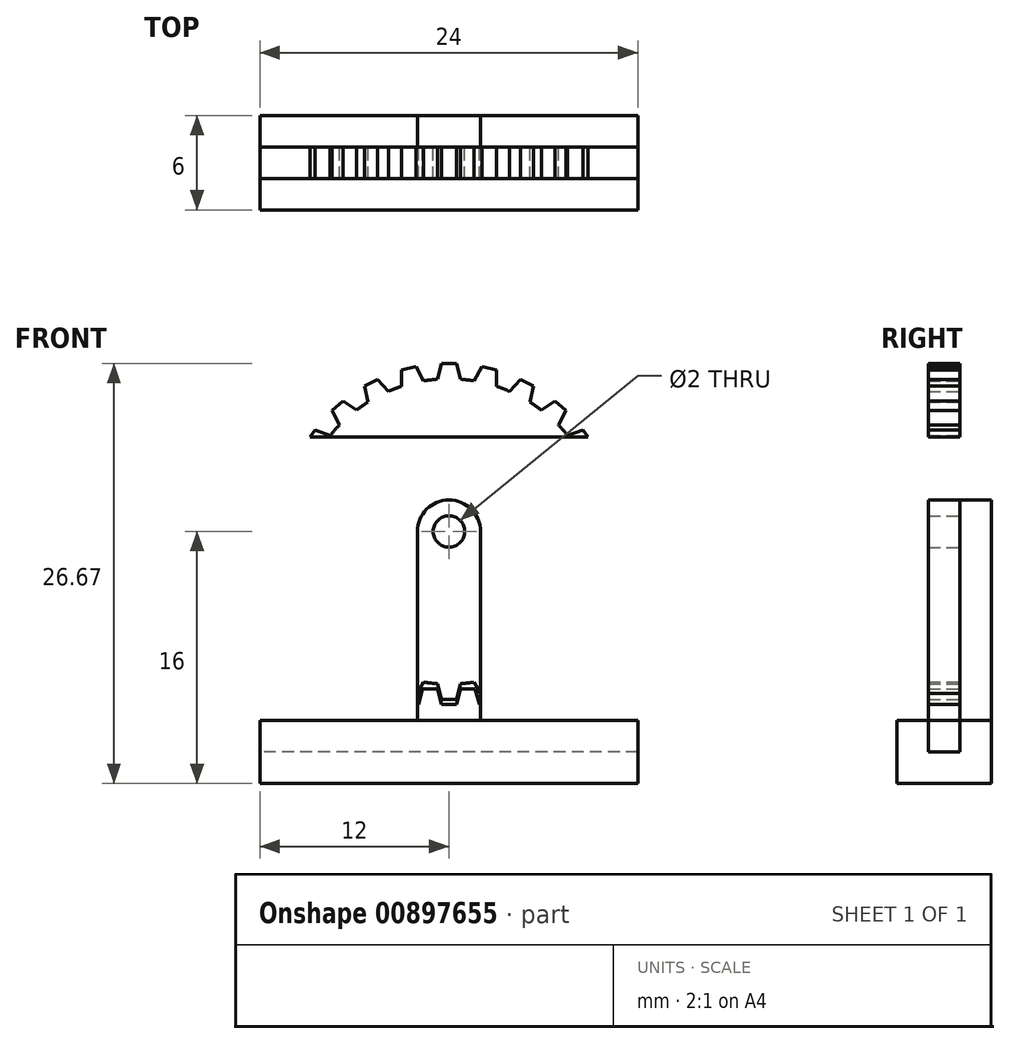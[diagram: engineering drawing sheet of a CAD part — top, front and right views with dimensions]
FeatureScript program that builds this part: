
annotation { "Feature Type Name" : "Feature", "Feature Type Description" : "" }
export const myFeature = defineFeature(function(context is Context, id is Id, definition is map)
    precondition{}
    {
        {
            var Q0;
            Q0=qCreatedBy(makeId("Right.planeOp"),FACE);
            var sketch = newSketch(context, id + "F0", { "sketchPlane" : qUnion([Q0])});
            skLineSegment(sketch, "E0", {"start": v(0, 2) * mm, "end": v(-2, 2) * mm});
            skLineSegment(sketch, "E1", {"start": v(-2, 2) * mm, "end": v(-2, -2) * mm});
            skLineSegment(sketch, "E2", {"start": v(-2, -2) * mm, "end": v(4, -2) * mm});
            skLineSegment(sketch, "E3", {"start": v(4, -2) * mm, "end": v(4, 20) * mm});
            skLineSegment(sketch, "E4", {"start": v(4, 20) * mm, "end": v(2, 20) * mm});
            skLineSegment(sketch, "E5", {"start": v(2, 20) * mm, "end": v(2, 0) * mm});
            skLineSegment(sketch, "E6", {"start": v(2, 0) * mm, "end": v(0, 0) * mm});
            skLineSegment(sketch, "E7", {"start": v(0, 0) * mm, "end": v(0, 2) * mm});
            skSolve(sketch);
        }
        {
            var Q0;
            Q0 = qSketchRegion(id + "F0", true);
            extrude(context, id + "F1", {"entities" : qUnion([Q0]), "endBound" : BoundingType.SYMMETRIC, "depth" : 24 * mm, "offsetDistance" : 25 * mm});
        }
        {
            var Q0;
            Q0=makeQuery(id+"F1.opExtrude","SWEPT_FACE",FACE,{"disambiguationData":[OSD([sQuery(id+"F0.wireOp",EDGE,"E5")])]});
            var sketch = newSketch(context, id + "F2", { "sketchPlane" : qUnion([Q0])});
            skLineSegment(sketch, "E8", {"start": v(-12, 0) * mm, "end": v(12, 0) * mm});
            skLineSegment(sketch, "E9", {"start": v(-12, 3) * mm, "end": v(-11.53, 3) * mm});
            skLineSegment(sketch, "E10", {"start": v(-11.53, 3) * mm, "end": v(-11.27, 4) * mm});
            skLineSegment(sketch, "E11", {"start": v(-11.27, 4) * mm, "end": v(-10.8, 4) * mm});
            skLineSegment(sketch, "E12", {"start": v(-10.8, 4) * mm, "end": v(-10.8, 0) * mm, "construction": true});
            skLineSegment(sketch, "E13.MirrorCS", {"start": v(-10.33, 4) * mm, "end": v(-10.8, 4) * mm});
            skLineSegment(sketch, "E14.MirrorCS", {"start": v(-10.07, 3) * mm, "end": v(-10.33, 4) * mm});
            skLineSegment(sketch, "E15.MirrorCS", {"start": v(-9.6, 3) * mm, "end": v(-10.07, 3) * mm});
            skLineSegment(sketch, "E16.1.0.0", {"start": v(-9.6, 3) * mm, "end": v(-9.13, 3) * mm});
            skLineSegment(sketch, "E16.1.0.1", {"start": v(-9.13, 3) * mm, "end": v(-8.87, 4) * mm});
            skLineSegment(sketch, "E16.1.0.2", {"start": v(-8.87, 4) * mm, "end": v(-8.4, 4) * mm});
            skLineSegment(sketch, "E16.1.0.3", {"start": v(-7.93, 4) * mm, "end": v(-8.4, 4) * mm});
            skLineSegment(sketch, "E16.1.0.4", {"start": v(-7.67, 3) * mm, "end": v(-7.93, 4) * mm});
            skLineSegment(sketch, "E16.1.0.5", {"start": v(-7.2, 3) * mm, "end": v(-7.67, 3) * mm});
            skLineSegment(sketch, "E16.2.0.0", {"start": v(-7.2, 3) * mm, "end": v(-6.73, 3) * mm});
            skLineSegment(sketch, "E16.2.0.1", {"start": v(-6.73, 3) * mm, "end": v(-6.47, 4) * mm});
            skLineSegment(sketch, "E16.2.0.2", {"start": v(-6.47, 4) * mm, "end": v(-6, 4) * mm});
            skLineSegment(sketch, "E16.2.0.3", {"start": v(-5.53, 4) * mm, "end": v(-6, 4) * mm});
            skLineSegment(sketch, "E16.2.0.4", {"start": v(-5.27, 3) * mm, "end": v(-5.53, 4) * mm});
            skLineSegment(sketch, "E16.2.0.5", {"start": v(-4.8, 3) * mm, "end": v(-5.27, 3) * mm});
            skLineSegment(sketch, "E16.direction1", {"start": v(-12, 3) * mm, "end": v(-9.6, 3) * mm, "construction": true});
            skLineSegment(sketch, "E17.0.3.0", {"start": v(-4.8, 3) * mm, "end": v(-4.33, 3) * mm});
            skLineSegment(sketch, "E17.3.3.0", {"start": v(-4.33, 3) * mm, "end": v(-4.07, 4) * mm});
            skLineSegment(sketch, "E17.6.3.0", {"start": v(-4.07, 4) * mm, "end": v(-3.6, 4) * mm});
            skLineSegment(sketch, "E17.9.3.0", {"start": v(-3.13, 4) * mm, "end": v(-3.6, 4) * mm});
            skLineSegment(sketch, "E17.12.3.0", {"start": v(-2.87, 3) * mm, "end": v(-3.13, 4) * mm});
            skLineSegment(sketch, "E17.15.3.0", {"start": v(-2.4, 3) * mm, "end": v(-2.87, 3) * mm});
            skLineSegment(sketch, "E17.0.4.0", {"start": v(-2.4, 3) * mm, "end": v(-1.93, 3) * mm});
            skLineSegment(sketch, "E17.3.4.0", {"start": v(-1.93, 3) * mm, "end": v(-1.67, 4) * mm});
            skLineSegment(sketch, "E17.6.4.0", {"start": v(-1.67, 4) * mm, "end": v(-1.2, 4) * mm});
            skLineSegment(sketch, "E17.9.4.0", {"start": v(-0.73, 4) * mm, "end": v(-1.2, 4) * mm});
            skLineSegment(sketch, "E17.12.4.0", {"start": v(-0.47, 3) * mm, "end": v(-0.73, 4) * mm});
            skLineSegment(sketch, "E17.15.4.0", {"start": v(0, 3) * mm, "end": v(-0.47, 3) * mm});
            skLineSegment(sketch, "E17.0.5.0", {"start": v(0, 3) * mm, "end": v(0.47, 3) * mm});
            skLineSegment(sketch, "E17.3.5.0", {"start": v(0.47, 3) * mm, "end": v(0.73, 4) * mm});
            skLineSegment(sketch, "E17.6.5.0", {"start": v(0.73, 4) * mm, "end": v(1.2, 4) * mm});
            skLineSegment(sketch, "E17.9.5.0", {"start": v(1.67, 4) * mm, "end": v(1.2, 4) * mm});
            skLineSegment(sketch, "E17.12.5.0", {"start": v(1.93, 3) * mm, "end": v(1.67, 4) * mm});
            skLineSegment(sketch, "E17.15.5.0", {"start": v(2.4, 3) * mm, "end": v(1.93, 3) * mm});
            skLineSegment(sketch, "E17.0.6.0", {"start": v(2.4, 3) * mm, "end": v(2.87, 3) * mm});
            skLineSegment(sketch, "E17.3.6.0", {"start": v(2.87, 3) * mm, "end": v(3.13, 4) * mm});
            skLineSegment(sketch, "E17.6.6.0", {"start": v(3.13, 4) * mm, "end": v(3.6, 4) * mm});
            skLineSegment(sketch, "E17.9.6.0", {"start": v(4.07, 4) * mm, "end": v(3.6, 4) * mm});
            skLineSegment(sketch, "E17.12.6.0", {"start": v(4.33, 3) * mm, "end": v(4.07, 4) * mm});
            skLineSegment(sketch, "E17.15.6.0", {"start": v(4.8, 3) * mm, "end": v(4.33, 3) * mm});
            skLineSegment(sketch, "E17.0.7.0", {"start": v(4.8, 3) * mm, "end": v(5.27, 3) * mm});
            skLineSegment(sketch, "E17.3.7.0", {"start": v(5.27, 3) * mm, "end": v(5.53, 4) * mm});
            skLineSegment(sketch, "E17.6.7.0", {"start": v(5.53, 4) * mm, "end": v(6, 4) * mm});
            skLineSegment(sketch, "E17.9.7.0", {"start": v(6.47, 4) * mm, "end": v(6, 4) * mm});
            skLineSegment(sketch, "E17.12.7.0", {"start": v(6.73, 3) * mm, "end": v(6.47, 4) * mm});
            skLineSegment(sketch, "E17.15.7.0", {"start": v(7.2, 3) * mm, "end": v(6.73, 3) * mm});
            skLineSegment(sketch, "E17.0.8.0", {"start": v(7.2, 3) * mm, "end": v(7.67, 3) * mm});
            skLineSegment(sketch, "E17.3.8.0", {"start": v(7.67, 3) * mm, "end": v(7.93, 4) * mm});
            skLineSegment(sketch, "E17.6.8.0", {"start": v(7.93, 4) * mm, "end": v(8.4, 4) * mm});
            skLineSegment(sketch, "E17.9.8.0", {"start": v(8.87, 4) * mm, "end": v(8.4, 4) * mm});
            skLineSegment(sketch, "E17.12.8.0", {"start": v(9.13, 3) * mm, "end": v(8.87, 4) * mm});
            skLineSegment(sketch, "E17.15.8.0", {"start": v(9.6, 3) * mm, "end": v(9.13, 3) * mm});
            skLineSegment(sketch, "E17.0.9.0", {"start": v(9.6, 3) * mm, "end": v(10.07, 3) * mm});
            skLineSegment(sketch, "E17.3.9.0", {"start": v(10.07, 3) * mm, "end": v(10.33, 4) * mm});
            skLineSegment(sketch, "E17.6.9.0", {"start": v(10.33, 4) * mm, "end": v(10.8, 4) * mm});
            skLineSegment(sketch, "E17.9.9.0", {"start": v(11.27, 4) * mm, "end": v(10.8, 4) * mm});
            skLineSegment(sketch, "E17.12.9.0", {"start": v(11.53, 3) * mm, "end": v(11.27, 4) * mm});
            skLineSegment(sketch, "E17.15.9.0", {"start": v(12, 3) * mm, "end": v(11.53, 3) * mm});
            skLineSegment(sketch, "E18", {"start": v(-12, 3) * mm, "end": v(-12, 0) * mm});
            skLineSegment(sketch, "E19", {"start": v(12, 3) * mm, "end": v(12, 0) * mm});
            skSolve(sketch);
        }
        {
            var Q0;
            Q0 = qSketchRegion(id + "F2", true);
            extrude(context, id + "F3", {"entities" : qUnion([Q0]), "depth" : 2 * mm, "offsetDistance" : 25 * mm});
        }
        {
            var Q0;
            Q0=makeQuery(id+"F1.opExtrude","SWEPT_FACE",FACE,{"disambiguationData":[OSD([sQuery(id+"F0.wireOp",EDGE,"E5")])]});
            var sketch = newSketch(context, id + "F4", { "sketchPlane" : qUnion([Q0])});
            skCircle(sketch, "E20", {"center": v(0, 14) * mm, "radius": 1 * mm});
            skSolve(sketch);
        }
        {
            var Q0;
            Q0 = qSketchRegion(id + "F4", true);
            extrude(context, id + "F5", {"entities" : qUnion([Q0]), "operationType" : NewBodyOperationType.ADD, "depth" : 2 * mm, "offsetDistance" : 25 * mm});
        }
        {
            var Q0;
            Q0=makeQuery(id+"F1.opExtrude","SWEPT_FACE",FACE,{"disambiguationData":[OSD([sQuery(id+"F0.wireOp",EDGE,"E5")])]});
            var sketch = newSketch(context, id + "F6", { "sketchPlane" : qUnion([Q0])});
            skCircle(sketch, "E21.0", {"center": v(0, 14) * mm, "radius": 1 * mm});
            skCircle(sketch, "E22", {"center": v(0, 14) * mm, "radius": 9.7 * mm});
            skLineSegment(sketch, "E23", {"start": v(0.73, 4.33) * mm, "end": v(0.47, 3.33) * mm});
            skLineSegment(sketch, "E24", {"start": v(0.47, 3.33) * mm, "end": v(-0.47, 3.33) * mm});
            skLineSegment(sketch, "E25.MirrorCS", {"start": v(-0.73, 4.33) * mm, "end": v(-0.47, 3.33) * mm});
            skLineSegment(sketch, "E26.1.0", {"start": v(3.03, 4.78) * mm, "end": v(3, 3.75) * mm});
            skLineSegment(sketch, "E26.1.1", {"start": v(3, 3.75) * mm, "end": v(2.1, 3.53) * mm});
            skLineSegment(sketch, "E26.1.2", {"start": v(1.6, 4.43) * mm, "end": v(2.1, 3.53) * mm});
            skLineSegment(sketch, "E26.2.0", {"start": v(5.14, 5.78) * mm, "end": v(5.37, 4.77) * mm});
            skLineSegment(sketch, "E26.2.1", {"start": v(5.37, 4.77) * mm, "end": v(4.55, 4.33) * mm});
            skLineSegment(sketch, "E26.2.2", {"start": v(3.84, 5.1) * mm, "end": v(4.55, 4.33) * mm});
            skLineSegment(sketch, "E27.2.3.0", {"start": v(6.96, 7.25) * mm, "end": v(7.43, 6.32) * mm});
            skLineSegment(sketch, "E27.3.3.0", {"start": v(7.43, 6.32) * mm, "end": v(6.73, 5.7) * mm});
            skLineSegment(sketch, "E27.6.3.0", {"start": v(5.86, 6.27) * mm, "end": v(6.73, 5.7) * mm});
            skLineSegment(sketch, "E27.2.4.0", {"start": v(8.38, 9.1) * mm, "end": v(9.05, 8.32) * mm});
            skLineSegment(sketch, "E27.3.4.0", {"start": v(9.05, 8.32) * mm, "end": v(8.52, 7.55) * mm});
            skLineSegment(sketch, "E27.6.4.0", {"start": v(7.54, 7.9) * mm, "end": v(8.52, 7.55) * mm});
            skLineSegment(sketch, "E27.2.5.0", {"start": v(9.3, 11.26) * mm, "end": v(10.14, 10.65) * mm});
            skLineSegment(sketch, "E27.3.5.0", {"start": v(10.14, 10.65) * mm, "end": v(9.81, 9.78) * mm});
            skLineSegment(sketch, "E27.6.5.0", {"start": v(8.78, 9.88) * mm, "end": v(9.81, 9.78) * mm});
            skLineSegment(sketch, "E27.2.6.0", {"start": v(9.7, 13.56) * mm, "end": v(10.65, 13.18) * mm});
            skLineSegment(sketch, "E27.3.6.0", {"start": v(10.65, 13.18) * mm, "end": v(10.54, 12.25) * mm});
            skLineSegment(sketch, "E27.6.6.0", {"start": v(9.51, 12.1) * mm, "end": v(10.54, 12.25) * mm});
            skLineSegment(sketch, "E27.2.7.0", {"start": v(9.51, 15.9) * mm, "end": v(10.54, 15.75) * mm});
            skLineSegment(sketch, "E27.3.7.0", {"start": v(10.54, 15.75) * mm, "end": v(10.65, 14.82) * mm});
            skLineSegment(sketch, "E27.6.7.0", {"start": v(9.7, 14.44) * mm, "end": v(10.65, 14.82) * mm});
            skLineSegment(sketch, "E27.2.8.0", {"start": v(8.78, 18.12) * mm, "end": v(9.81, 18.22) * mm});
            skLineSegment(sketch, "E27.3.8.0", {"start": v(9.81, 18.22) * mm, "end": v(10.14, 17.35) * mm});
            skLineSegment(sketch, "E27.6.8.0", {"start": v(9.3, 16.74) * mm, "end": v(10.14, 17.35) * mm});
            skLineSegment(sketch, "E27.2.9.0", {"start": v(7.54, 20.1) * mm, "end": v(8.52, 20.45) * mm});
            skLineSegment(sketch, "E27.3.9.0", {"start": v(8.52, 20.45) * mm, "end": v(9.05, 19.68) * mm});
            skLineSegment(sketch, "E27.6.9.0", {"start": v(8.38, 18.9) * mm, "end": v(9.05, 19.68) * mm});
            skLineSegment(sketch, "E27.2.10.0", {"start": v(5.86, 21.73) * mm, "end": v(6.73, 22.3) * mm});
            skLineSegment(sketch, "E27.3.10.0", {"start": v(6.73, 22.3) * mm, "end": v(7.43, 21.68) * mm});
            skLineSegment(sketch, "E27.6.10.0", {"start": v(6.96, 20.75) * mm, "end": v(7.43, 21.68) * mm});
            skLineSegment(sketch, "E27.2.11.0", {"start": v(3.84, 22.9) * mm, "end": v(4.55, 23.67) * mm});
            skLineSegment(sketch, "E27.3.11.0", {"start": v(4.55, 23.67) * mm, "end": v(5.37, 23.23) * mm});
            skLineSegment(sketch, "E27.6.11.0", {"start": v(5.14, 22.22) * mm, "end": v(5.37, 23.23) * mm});
            skLineSegment(sketch, "E27.2.12.0", {"start": v(1.6, 23.57) * mm, "end": v(2.1, 24.47) * mm});
            skLineSegment(sketch, "E27.3.12.0", {"start": v(2.1, 24.47) * mm, "end": v(3, 24.25) * mm});
            skLineSegment(sketch, "E27.6.12.0", {"start": v(3.03, 23.22) * mm, "end": v(3, 24.25) * mm});
            skLineSegment(sketch, "E27.2.13.0", {"start": v(-0.73, 23.67) * mm, "end": v(-0.47, 24.67) * mm});
            skLineSegment(sketch, "E27.3.13.0", {"start": v(-0.47, 24.67) * mm, "end": v(0.47, 24.67) * mm});
            skLineSegment(sketch, "E27.6.13.0", {"start": v(0.73, 23.67) * mm, "end": v(0.47, 24.67) * mm});
            skLineSegment(sketch, "E27.2.14.0", {"start": v(-3.03, 23.22) * mm, "end": v(-3, 24.25) * mm});
            skLineSegment(sketch, "E27.3.14.0", {"start": v(-3, 24.25) * mm, "end": v(-2.1, 24.47) * mm});
            skLineSegment(sketch, "E27.6.14.0", {"start": v(-1.6, 23.57) * mm, "end": v(-2.1, 24.47) * mm});
            skLineSegment(sketch, "E27.2.15.0", {"start": v(-5.14, 22.22) * mm, "end": v(-5.37, 23.23) * mm});
            skLineSegment(sketch, "E27.3.15.0", {"start": v(-5.37, 23.23) * mm, "end": v(-4.55, 23.67) * mm});
            skLineSegment(sketch, "E27.6.15.0", {"start": v(-3.84, 22.9) * mm, "end": v(-4.55, 23.67) * mm});
            skLineSegment(sketch, "E27.2.16.0", {"start": v(-6.96, 20.75) * mm, "end": v(-7.43, 21.68) * mm});
            skLineSegment(sketch, "E27.3.16.0", {"start": v(-7.43, 21.68) * mm, "end": v(-6.73, 22.3) * mm});
            skLineSegment(sketch, "E27.6.16.0", {"start": v(-5.86, 21.73) * mm, "end": v(-6.73, 22.3) * mm});
            skLineSegment(sketch, "E27.2.17.0", {"start": v(-8.38, 18.9) * mm, "end": v(-9.05, 19.68) * mm});
            skLineSegment(sketch, "E27.3.17.0", {"start": v(-9.05, 19.68) * mm, "end": v(-8.52, 20.45) * mm});
            skLineSegment(sketch, "E27.6.17.0", {"start": v(-7.54, 20.1) * mm, "end": v(-8.52, 20.45) * mm});
            skLineSegment(sketch, "E27.2.18.0", {"start": v(-9.3, 16.74) * mm, "end": v(-10.14, 17.35) * mm});
            skLineSegment(sketch, "E27.3.18.0", {"start": v(-10.14, 17.35) * mm, "end": v(-9.81, 18.22) * mm});
            skLineSegment(sketch, "E27.6.18.0", {"start": v(-8.78, 18.12) * mm, "end": v(-9.81, 18.22) * mm});
            skLineSegment(sketch, "E27.2.19.0", {"start": v(-9.7, 14.44) * mm, "end": v(-10.65, 14.82) * mm});
            skLineSegment(sketch, "E27.3.19.0", {"start": v(-10.65, 14.82) * mm, "end": v(-10.54, 15.75) * mm});
            skLineSegment(sketch, "E27.6.19.0", {"start": v(-9.51, 15.9) * mm, "end": v(-10.54, 15.75) * mm});
            skLineSegment(sketch, "E28.2.20.0", {"start": v(-9.51, 12.1) * mm, "end": v(-10.54, 12.25) * mm});
            skLineSegment(sketch, "E28.3.20.0", {"start": v(-10.54, 12.25) * mm, "end": v(-10.65, 13.18) * mm});
            skLineSegment(sketch, "E28.6.20.0", {"start": v(-9.7, 13.56) * mm, "end": v(-10.65, 13.18) * mm});
            skLineSegment(sketch, "E28.2.21.0", {"start": v(-8.78, 9.88) * mm, "end": v(-9.81, 9.78) * mm});
            skLineSegment(sketch, "E28.3.21.0", {"start": v(-9.81, 9.78) * mm, "end": v(-10.14, 10.65) * mm});
            skLineSegment(sketch, "E28.6.21.0", {"start": v(-9.3, 11.26) * mm, "end": v(-10.14, 10.65) * mm});
            skLineSegment(sketch, "E28.2.22.0", {"start": v(-7.54, 7.9) * mm, "end": v(-8.52, 7.55) * mm});
            skLineSegment(sketch, "E28.3.22.0", {"start": v(-8.52, 7.55) * mm, "end": v(-9.05, 8.32) * mm});
            skLineSegment(sketch, "E28.6.22.0", {"start": v(-8.38, 9.1) * mm, "end": v(-9.05, 8.32) * mm});
            skLineSegment(sketch, "E28.2.23.0", {"start": v(-5.86, 6.27) * mm, "end": v(-6.73, 5.7) * mm});
            skLineSegment(sketch, "E28.3.23.0", {"start": v(-6.73, 5.7) * mm, "end": v(-7.43, 6.32) * mm});
            skLineSegment(sketch, "E28.6.23.0", {"start": v(-6.96, 7.25) * mm, "end": v(-7.43, 6.32) * mm});
            skLineSegment(sketch, "E29.2.24.0", {"start": v(-3.84, 5.1) * mm, "end": v(-4.55, 4.33) * mm});
            skLineSegment(sketch, "E29.3.24.0", {"start": v(-4.55, 4.33) * mm, "end": v(-5.37, 4.77) * mm});
            skLineSegment(sketch, "E29.6.24.0", {"start": v(-5.14, 5.78) * mm, "end": v(-5.37, 4.77) * mm});
            skLineSegment(sketch, "E29.2.25.0", {"start": v(-1.6, 4.43) * mm, "end": v(-2.1, 3.53) * mm});
            skLineSegment(sketch, "E29.3.25.0", {"start": v(-2.1, 3.53) * mm, "end": v(-3, 3.75) * mm});
            skLineSegment(sketch, "E29.6.25.0", {"start": v(-3.03, 4.78) * mm, "end": v(-3, 3.75) * mm});
            skSolve(sketch);
        }
        {
            var Q0;
            Q0 = qSketchRegion(id + "F6", true);
            extrude(context, id + "F7", {"entities" : qUnion([Q0]), "depth" : 2 * mm, "offsetDistance" : 25 * mm});
        }
        {
            var Q0;
            Q0=makeQuery(id+"F1.opExtrude","SWEPT_FACE",FACE,{"disambiguationData":[OSD([sQuery(id+"F0.wireOp",EDGE,"E3")])]});
            var sketch = newSketch(context, id + "F8", { "sketchPlane" : qUnion([Q0])});
            skLineSegment(sketch, "E30", {"start": v(12, 2) * mm, "end": v(2, 2) * mm});
            skLineSegment(sketch, "E31", {"start": v(2, 2) * mm, "end": v(2, 14) * mm});
            skArc(sketch, "E32", {"start": v(2, 14) * mm, "mid": v(0, 16) * mm, "end": v(-2, 14) * mm});
            skLineSegment(sketch, "E33.MirrorCS", {"start": v(-2, 2) * mm, "end": v(-2, 14) * mm});
            skLineSegment(sketch, "E34.MirrorCS", {"start": v(-12, 2) * mm, "end": v(-2, 2) * mm});
            skLineSegment(sketch, "E35", {"start": v(12, 2) * mm, "end": v(12, 20) * mm});
            skLineSegment(sketch, "E36", {"start": v(12, 20) * mm, "end": v(-12, 20) * mm});
            skLineSegment(sketch, "E37", {"start": v(-12, 20) * mm, "end": v(-12, 2) * mm});
            skSolve(sketch);
        }
        {
            var Q0;
            Q0 = qSketchRegion(id + "F8", true);
            extrude(context, id + "F9", {"entities" : qUnion([Q0]), "operationType" : NewBodyOperationType.REMOVE, "oppositeDirection" : true, "depth" : 25 * mm, "offsetDistance" : 25 * mm});
        }
    });
